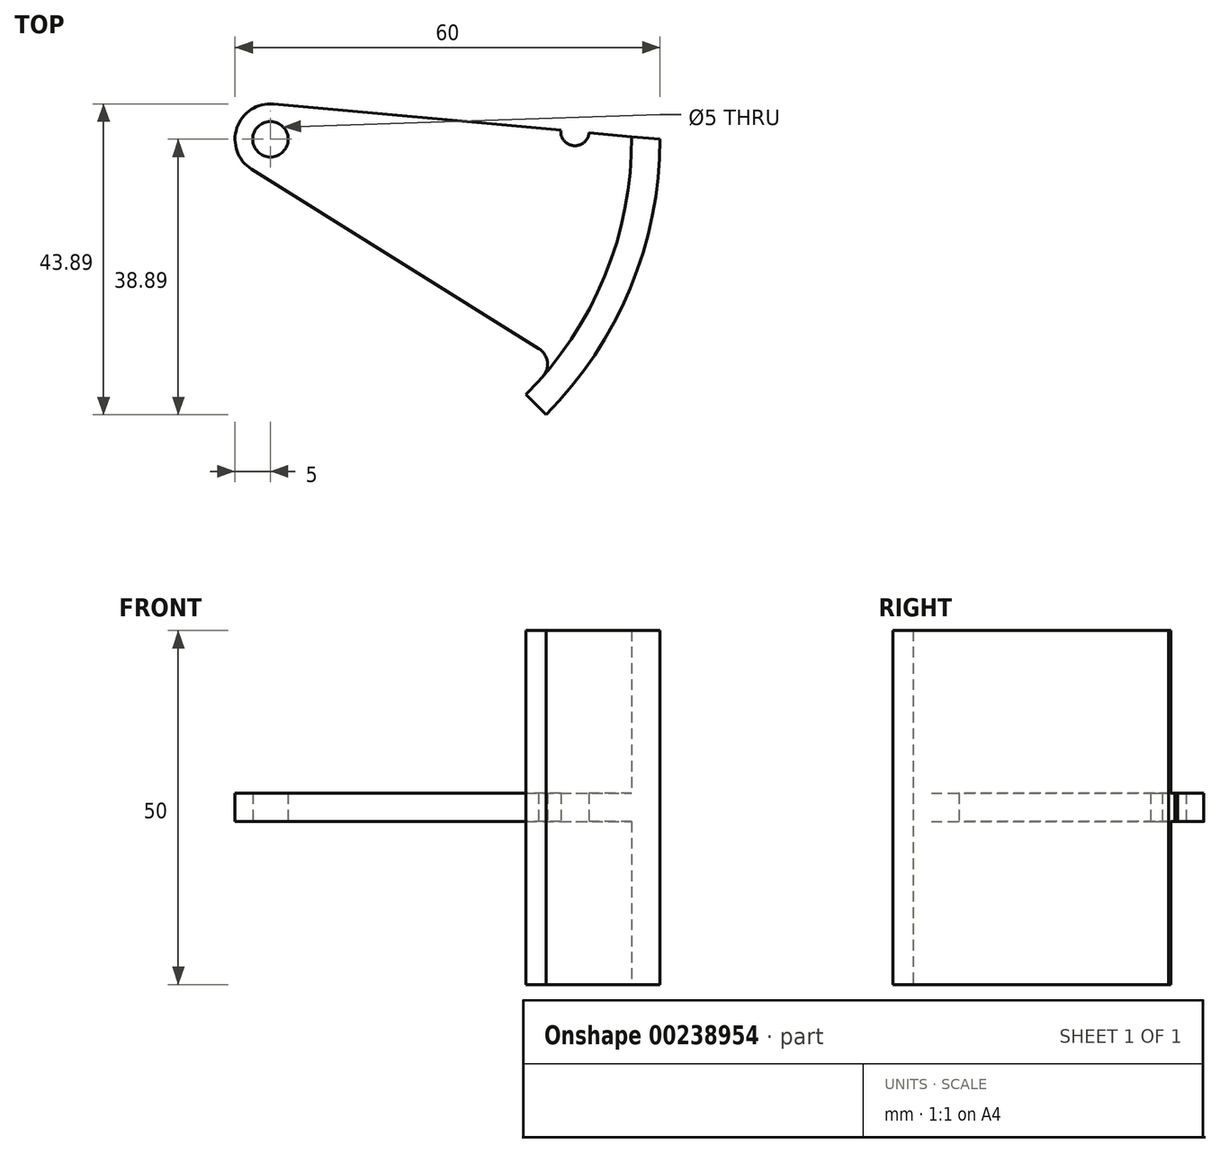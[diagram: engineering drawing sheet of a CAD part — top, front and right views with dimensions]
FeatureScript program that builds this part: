
annotation { "Feature Type Name" : "Feature", "Feature Type Description" : "" }
export const myFeature = defineFeature(function(context is Context, id is Id, definition is map)
    precondition{}
    {
        {
            var Q0;
            Q0=qCreatedBy(makeId("Top.planeOp"),FACE);
            var sketch = newSketch(context, id + "F0", { "sketchPlane" : qUnion([Q0])});
            skCircle(sketch, "E0", {"center": v(0, 0) * mm, "radius": 2.5 * mm});
            skArc(sketch, "E1", {"start": v(0.45, 4.98) * mm, "mid": v(-4.74, 1.6) * mm, "end": v(-2.65, -4.24) * mm});
            skLineSegment(sketch, "E2", {"start": v(-13.18, 5) * mm, "end": v(38.9, 5) * mm, "construction": true});
            skArc(sketch, "E3", {"start": v(38.89, -38.89) * mm, "mid": v(50.81, -21.05) * mm, "end": v(55, 0) * mm});
            skArc(sketch, "E4", {"start": v(3.73, 3.33) * mm, "mid": v(7.1, 0.87) * mm, "end": v(11.18, 0) * mm, "construction": true});
            skLineSegment(sketch, "E5.trimOffspring", {"start": v(11.18, 0) * mm, "end": v(55, 0) * mm, "construction": true});
            skPoint(sketch, "E6", {"position": v(55, 0) * mm});
            skArc(sketch, "E7", {"start": v(36.06, -36.06) * mm, "mid": v(37.3, -34.78) * mm, "end": v(38.5, -33.46) * mm});
            skLineSegment(sketch, "E8", {"start": v(-2.65, -4.24) * mm, "end": v(37.85, -29.55) * mm});
            skLineSegment(sketch, "E9", {"start": v(26.3, -25.87) * mm, "end": v(45.8, -38.05) * mm, "construction": true});
            skPoint(sketch, "E10", {"position": v(40.4, -31.14) * mm});
            skCircle(sketch, "E11", {"center": v(40.4, -31.14) * mm, "radius": 3 * mm, "construction": true});
            skPoint(sketch, "E12", {"position": v(37.85, -29.55) * mm});
            skArc(sketch, "E13.trimOffspring", {"start": v(40.4, -31.14) * mm, "mid": v(48.28, -16.45) * mm, "end": v(51, 0) * mm, "construction": true});
            skLineSegment(sketch, "E14.trimOffspring", {"start": v(40.4, -31.14) * mm, "end": v(64.64, -46.29) * mm});
            skArc(sketch, "E15", {"start": v(38.5, -33.46) * mm, "mid": v(39.09, -31.35) * mm, "end": v(37.85, -29.55) * mm});
            skLineSegment(sketch, "E16", {"start": v(0, 0) * mm, "end": v(15.72, -15.72) * mm});
            skLineSegment(sketch, "E17.trimOffspring", {"start": v(36.06, -36.06) * mm, "end": v(38.89, -38.89) * mm});
            skPoint(sketch, "E18", {"position": v(36.06, -36.06) * mm});
            skPoint(sketch, "E19", {"position": v(38.89, -38.89) * mm});
            skLineSegment(sketch, "E20", {"start": v(20.9, -6) * mm, "end": v(67.18, -6) * mm, "construction": true});
            skCircle(sketch, "E21", {"center": v(0, 0) * mm, "radius": 43 * mm, "construction": true});
            skCircle(sketch, "E22", {"center": v(42.58, -6) * mm, "radius": 2 * mm, "construction": true});
            skLineSegment(sketch, "E23", {"start": v(55, 0) * mm, "end": v(44.98, 0.91) * mm});
            skArc(sketch, "E24", {"start": v(41, 1.28) * mm, "mid": v(42.8, -0.9) * mm, "end": v(44.98, 0.91) * mm});
            skLineSegment(sketch, "E25.trimOffspring", {"start": v(41, 1.28) * mm, "end": v(0.23, 5) * mm});
            skSolve(sketch);
        }
        {
            var Q0;
            Q0=qCreatedBy(makeId("Top.planeOp"),FACE);
            var sketch = newSketch(context, id + "F1", { "sketchPlane" : qUnion([Q0])});
            skArc(sketch, "E26", {"start": v(38.9, -38.9) * mm, "mid": v(50.81, -21.05) * mm, "end": v(55, 0) * mm});
            skArc(sketch, "E27", {"start": v(36.06, -36.06) * mm, "mid": v(47.19, -19.35) * mm, "end": v(51, 0.37) * mm});
            skLineSegment(sketch, "E28", {"start": v(55, 0) * mm, "end": v(55, 0) * mm});
            skLineSegment(sketch, "E29", {"start": v(36.06, -36.06) * mm, "end": v(38.9, -38.9) * mm});
            skLineSegment(sketch, "E30.0", {"start": v(55, 0) * mm, "end": v(51, 0.37) * mm});
            skCircle(sketch, "E31", {"center": v(0, 0) * mm, "radius": 5 * mm, "construction": true});
            skSolve(sketch);
        }
        {
            var Q0;
            Q0=qSketchRegion(id+"F0",true);
            extrude(context, id + "F2", {"entities" : qUnion([Q0]), "depth" : 2 * mm, "hasSecondDirection" : true, "secondDirectionOppositeDirection" : true, "secondDirectionDepth" : 2 * mm});
        }
        {
            var Q0;
            Q0=qSketchRegion(id+"F1",true);
            extrude(context, id + "F3", {"entities" : qUnion([Q0]), "operationType" : NewBodyOperationType.ADD, "depth" : 25 * mm, "hasSecondDirection" : true, "secondDirectionOppositeDirection" : true, "secondDirectionDepth" : 25 * mm});
        }
    });
